# Revit family: xxxBody_Spray-Grohe-Rainshower-Aqua-26745_Series
name_source: partatom
category: Plumbing Fixtures
units: mm (PartAtom-declared; Revit-internal decimal feet)

## family parameters
Cut with Voids When Loaded = No
Host = Face
OmniClass Number = 23.45.05.14.17
OmniClass Title = Showers
Part Type = Normal
Room Calculation Point = No
Round Connector Dimension = Use Diameter
Shared = Yes

## types (2) — shared parameters
ASME A112.18.1/CSA B125.1 = Yes
Assembly Code = D2010710
CEC Compliant = Yes
CW Connection = No
CWFU = 3
CalGreen Compliant = Yes
Compliance Certifications = Massachusetts Plumbing Board Approved, CSA B125.1
Concealed Body (3 3/16"- 4 5/16") = 3 3/16"
Concealed Body Length = 3 3/16"
Default Elevation = 34"
Description = Rainshower™ Aqua Body Spray- 2 Sprays
Energy Policy Act of 1992 = Yes
Flow Rate = 0.9gpm (3.3 l/min)
HW Connection = No
HWFU = 3
Length = 7/8"
Manufacturer = Grohe
Price = Prices may vary. Please consult Manufacturer Representative for most up-to-date price list.
Tempered Water Connection = Yes
Tempered Water Connection Diameter = 1/2"
URL = https://www.grohe.us
Vent Connection = No
WFU = 4
Waste Connection = No
Width = 2 15/16"

## per-type parameters (varying)
| type | Finish | Material |
| 26744000 | Plastic-Grohe-000-Starlight Chrome | Plastic-Grohe-000-Starlight Chrome |
| 26745EN0 | Plastic-Grohe-Brushed Nickel Infinity Finish | Plastic-Grohe-Brushed Nickel Infinity Finish |

note: column(s) folded — value = type name in every type: Model

## geometry (parser evidence)
native form markers: Sweep x2
no freeform markers — native parametric forms only
